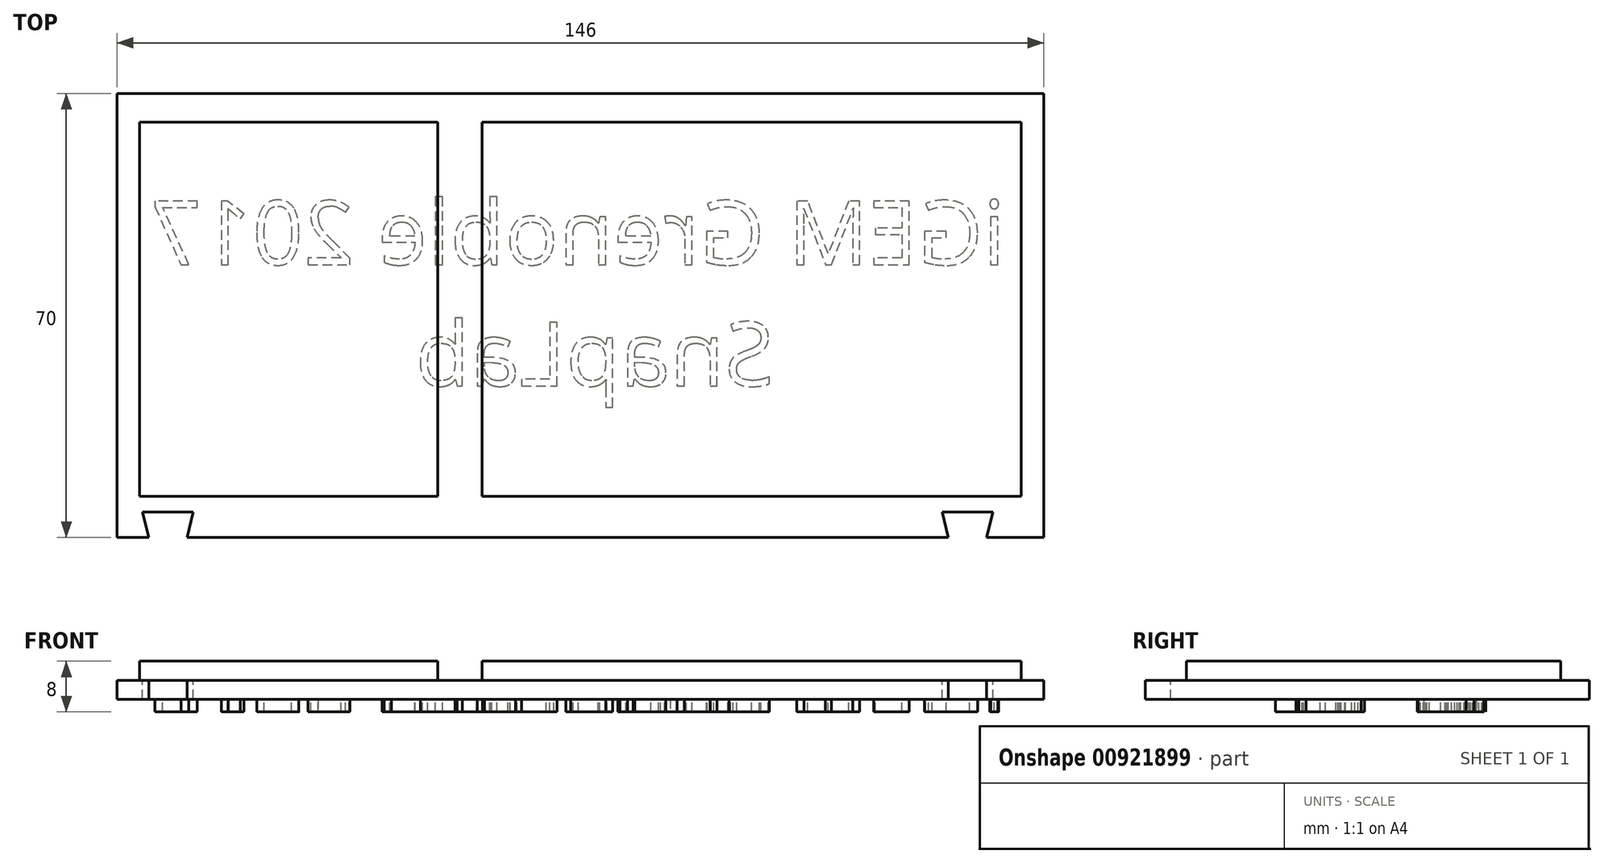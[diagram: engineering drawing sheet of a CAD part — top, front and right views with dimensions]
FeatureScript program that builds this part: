
annotation { "Feature Type Name" : "Feature", "Feature Type Description" : "" }
export const myFeature = defineFeature(function(context is Context, id is Id, definition is map)
    precondition{}
    {
        {
            var Q0;
            Q0=qCreatedBy(makeId("Top.planeOp"),FACE);
            var sketch = newSketch(context, id + "F0", { "sketchPlane" : qUnion([Q0])});
            skLineSegment(sketch, "E0.bottom", {"start": v(0, 0) * mm, "end": v(146, 0) * mm});
            skLineSegment(sketch, "E0.top", {"start": v(0, 70) * mm, "end": v(146, 70) * mm});
            skLineSegment(sketch, "E0.left", {"start": v(0, 0) * mm, "end": v(0, 70) * mm});
            skLineSegment(sketch, "E0.right", {"start": v(146, 0) * mm, "end": v(146, 70) * mm});
            skSolve(sketch);
        }
        {
            var Q0;
            Q0 = qSketchRegion(id + "F0", true);
            var Q1;
            Q1=makeQuery(id+"F0.imprint","IMPRINT",FACE,{"disambiguationData":[TD([[makeQuery(id+"F0.imprint","IMPRINT",EDGE,{"derivedFrom":sQuery(id+"F0.wireOp",EDGE,"E0.bottom")}),1.0]])]});
            extrude(context, id + "F1", {"entities" : qUnion([Q0, Q1]), "depth" : 3 * mm, "offsetDistance" : 25 * mm});
        }
        {
            var Q0;
            Q0=makeQuery(id+"F1.opExtrude","CAP_FACE",FACE,{"disambiguationData":[OSD([sQuery(id+"F0.wireOp",EDGE,"E0.bottom"),sQuery(id+"F0.wireOp",EDGE,"E0.top"),sQuery(id+"F0.wireOp",EDGE,"E0.left"),sQuery(id+"F0.wireOp",EDGE,"E0.right")])],"isStart":false});
            var sketch = newSketch(context, id + "F2", { "sketchPlane" : qUnion([Q0])});
            skLineSegment(sketch, "E1.bottom", {"start": v(3.5, 65.5) * mm, "end": v(50.5, 65.5) * mm});
            skLineSegment(sketch, "E1.top", {"start": v(3.5, 6.5) * mm, "end": v(50.5, 6.5) * mm});
            skLineSegment(sketch, "E1.left", {"start": v(3.5, 65.5) * mm, "end": v(3.5, 6.5) * mm});
            skLineSegment(sketch, "E1.right", {"start": v(50.5, 65.5) * mm, "end": v(50.5, 6.5) * mm});
            skLineSegment(sketch, "E2.bottom", {"start": v(57.5, 65.5) * mm, "end": v(142.5, 65.5) * mm});
            skLineSegment(sketch, "E2.top", {"start": v(57.5, 6.5) * mm, "end": v(142.5, 6.5) * mm});
            skLineSegment(sketch, "E2.left", {"start": v(57.5, 65.5) * mm, "end": v(57.5, 6.5) * mm});
            skLineSegment(sketch, "E2.right", {"start": v(142.5, 65.5) * mm, "end": v(142.5, 6.5) * mm});
            skLineSegment(sketch, "E3", {"start": v(4, 0) * mm, "end": v(4, 4) * mm});
            skLineSegment(sketch, "E4", {"start": v(4, 4) * mm, "end": v(12, 4) * mm});
            skLineSegment(sketch, "E5", {"start": v(12, 4) * mm, "end": v(12, 0) * mm});
            skLineSegment(sketch, "E6", {"start": v(138, 0) * mm, "end": v(138, 4) * mm});
            skLineSegment(sketch, "E7", {"start": v(138, 4) * mm, "end": v(130, 4) * mm});
            skLineSegment(sketch, "E8", {"start": v(130, 4) * mm, "end": v(130, 0) * mm});
            skLineSegment(sketch, "E9", {"start": v(4, 4) * mm, "end": v(5, 0) * mm});
            skLineSegment(sketch, "E10", {"start": v(5, 0) * mm, "end": v(4, 0) * mm});
            skLineSegment(sketch, "E11", {"start": v(12, 4) * mm, "end": v(11, 0) * mm});
            skLineSegment(sketch, "E12", {"start": v(11, 0) * mm, "end": v(12, 0) * mm});
            skLineSegment(sketch, "E13", {"start": v(138, 4) * mm, "end": v(137, 0) * mm});
            skLineSegment(sketch, "E14", {"start": v(137, 0) * mm, "end": v(138, 0) * mm});
            skLineSegment(sketch, "E15", {"start": v(130, 4) * mm, "end": v(131, 0) * mm});
            skLineSegment(sketch, "E16", {"start": v(131, 0) * mm, "end": v(130, 0) * mm});
            skSolve(sketch);
        }
        {
            var Q0;
            Q0=makeQuery(id+"F2.imprint","IMPRINT",FACE,{"disambiguationData":[TD([[makeQuery(id+"F2.imprint","IMPRINT",EDGE,{"derivedFrom":sQuery(id+"F2.wireOp",EDGE,"E1.bottom")}),-1.0]])]});
            var Q1;
            Q1=makeQuery(id+"F2.imprint","IMPRINT",FACE,{"disambiguationData":[TD([[makeQuery(id+"F2.imprint","IMPRINT",EDGE,{"derivedFrom":sQuery(id+"F2.wireOp",EDGE,"E2.bottom")}),-1.0]])]});
            extrude(context, id + "F3", {"entities" : qUnion([Q0, Q1]), "operationType" : NewBodyOperationType.ADD, "depth" : 3 * mm, "offsetDistance" : 25 * mm});
        }
        {
            var Q0;
            Q0=makeQuery(id+"F2.imprint","IMPRINT",FACE,{"disambiguationData":[TD([[makeQuery(id+"F2.imprint","IMPRINT",EDGE,{"derivedFrom":sQuery(id+"F2.wireOp",EDGE,"E4")}),-1.0]])]});
            extrude(context, id + "F4", {"entities" : qUnion([Q0]), "operationType" : NewBodyOperationType.REMOVE, "oppositeDirection" : true, "depth" : 3 * mm, "offsetDistance" : 25 * mm});
        }
        {
            var Q0;
            Q0=makeQuery(id+"F2.imprint","IMPRINT",FACE,{"disambiguationData":[TD([[makeQuery(id+"F2.imprint","IMPRINT",EDGE,{"derivedFrom":sQuery(id+"F2.wireOp",EDGE,"E7")}),1.0]])]});
            extrude(context, id + "F5", {"entities" : qUnion([Q0]), "operationType" : NewBodyOperationType.REMOVE, "oppositeDirection" : true, "depth" : 3 * mm, "offsetDistance" : 25 * mm});
        }
        {
            var Q0;
            Q0=makeQuery(id+"F1.opExtrude","CAP_FACE",FACE,{"disambiguationData":[OSD([sQuery(id+"F0.wireOp",EDGE,"E0.bottom"),sQuery(id+"F0.wireOp",EDGE,"E0.top"),sQuery(id+"F0.wireOp",EDGE,"E0.left"),sQuery(id+"F0.wireOp",EDGE,"E0.right")])],"isStart":true});
            var sketch = newSketch(context, id + "F6", { "sketchPlane" : qUnion([Q0])});
            skText(sketch, "E17", { "text": "iGEM Grenoble 2017\n          SnapLab", "fontName": "OpenSans-Regular.ttf"});
            const initialGuessF6  = {"E17": [0.14, -0.04303, -1, 0, 0.01012]};
            skSetInitialGuess(sketch, initialGuessF6);
            skSolve(sketch);
        }
        {
            var Q0;
            Q0=makeQuery(id+"F6.imprint","IMPRINT",FACE,{"disambiguationData":[TD([[makeQuery(id+"F6.imprint","IMPRINT",EDGE,{"derivedFrom":sQuery(id+"F6.wireOp",EDGE,"E17.sketch_text.stroke-4")}),-1.0]])]});
            var Q1;
            Q1=makeQuery(id+"F6.imprint","IMPRINT",FACE,{"disambiguationData":[TD([[makeQuery(id+"F6.imprint","IMPRINT",EDGE,{"derivedFrom":sQuery(id+"F6.wireOp",EDGE,"E17.sketch_text.stroke-12")}),-1.0]])]});
            var Q2;
            Q2=makeQuery(id+"F6.imprint","IMPRINT",FACE,{"disambiguationData":[TD([[makeQuery(id+"F6.imprint","IMPRINT",EDGE,{"derivedFrom":sQuery(id+"F6.wireOp",EDGE,"E17.sketch_text.stroke-32")}),-1.0]])]});
            var Q3;
            Q3=makeQuery(id+"F6.imprint","IMPRINT",FACE,{"disambiguationData":[TD([[makeQuery(id+"F6.imprint","IMPRINT",EDGE,{"derivedFrom":sQuery(id+"F6.wireOp",EDGE,"E17.sketch_text.stroke-0")}),-1.0]])]});
            var Q4;
            Q4=makeQuery(id+"F6.imprint","IMPRINT",FACE,{"disambiguationData":[TD([[makeQuery(id+"F6.imprint","IMPRINT",EDGE,{"derivedFrom":sQuery(id+"F6.wireOp",EDGE,"E17.sketch_text.stroke-44")}),-1.0]])]});
            var Q5;
            Q5=makeQuery(id+"F6.imprint","IMPRINT",FACE,{"disambiguationData":[TD([[makeQuery(id+"F6.imprint","IMPRINT",EDGE,{"derivedFrom":sQuery(id+"F6.wireOp",EDGE,"E17.sketch_text.stroke-62")}),-1.0]])]});
            var Q6;
            Q6=makeQuery(id+"F6.imprint","IMPRINT",FACE,{"disambiguationData":[TD([[makeQuery(id+"F6.imprint","IMPRINT",EDGE,{"derivedFrom":sQuery(id+"F6.wireOp",EDGE,"E17.sketch_text.stroke-82")}),-1.0]])]});
            var Q7;
            Q7=makeQuery(id+"F6.imprint","IMPRINT",FACE,{"disambiguationData":[TD([[makeQuery(id+"F6.imprint","IMPRINT",EDGE,{"derivedFrom":sQuery(id+"F6.wireOp",EDGE,"E17.sketch_text.stroke-95")}),-1.0]])]});
            var Q8;
            Q8=makeQuery(id+"F6.imprint","IMPRINT",FACE,{"disambiguationData":[TD([[makeQuery(id+"F6.imprint","IMPRINT",EDGE,{"derivedFrom":sQuery(id+"F6.wireOp",EDGE,"E17.sketch_text.stroke-114")}),-1.0]])]});
            var Q9;
            Q9=makeQuery(id+"F6.imprint","IMPRINT",FACE,{"disambiguationData":[TD([[makeQuery(id+"F6.imprint","IMPRINT",EDGE,{"derivedFrom":sQuery(id+"F6.wireOp",EDGE,"E17.sketch_text.stroke-131")}),-1.0]])]});
            var Q10;
            Q10=makeQuery(id+"F6.imprint","IMPRINT",FACE,{"disambiguationData":[TD([[makeQuery(id+"F6.imprint","IMPRINT",EDGE,{"derivedFrom":sQuery(id+"F6.wireOp",EDGE,"E17.sketch_text.stroke-148")}),-1.0]])]});
            var Q11;
            Q11=makeQuery(id+"F6.imprint","IMPRINT",FACE,{"disambiguationData":[TD([[makeQuery(id+"F6.imprint","IMPRINT",EDGE,{"derivedFrom":sQuery(id+"F6.wireOp",EDGE,"E17.sketch_text.stroke-171")}),-1.0]])]});
            var Q12;
            Q12=makeQuery(id+"F6.imprint","IMPRINT",FACE,{"disambiguationData":[TD([[makeQuery(id+"F6.imprint","IMPRINT",EDGE,{"derivedFrom":sQuery(id+"F6.wireOp",EDGE,"E17.sketch_text.stroke-175")}),-1.0]])]});
            var Q13;
            Q13=makeQuery(id+"F6.imprint","IMPRINT",FACE,{"disambiguationData":[TD([[makeQuery(id+"F6.imprint","IMPRINT",EDGE,{"derivedFrom":sQuery(id+"F6.wireOp",EDGE,"E17.sketch_text.stroke-194")}),-1.0]])]});
            var Q14;
            Q14=makeQuery(id+"F6.imprint","IMPRINT",FACE,{"disambiguationData":[TD([[makeQuery(id+"F6.imprint","IMPRINT",EDGE,{"derivedFrom":sQuery(id+"F6.wireOp",EDGE,"E17.sketch_text.stroke-214")}),-1.0]])]});
            var Q15;
            Q15=makeQuery(id+"F6.imprint","IMPRINT",FACE,{"disambiguationData":[TD([[makeQuery(id+"F6.imprint","IMPRINT",EDGE,{"derivedFrom":sQuery(id+"F6.wireOp",EDGE,"E17.sketch_text.stroke-230")}),-1.0]])]});
            var Q16;
            Q16=makeQuery(id+"F6.imprint","IMPRINT",FACE,{"disambiguationData":[TD([[makeQuery(id+"F6.imprint","IMPRINT",EDGE,{"derivedFrom":sQuery(id+"F6.wireOp",EDGE,"E17.sketch_text.stroke-239")}),-1.0]])]});
            var Q17;
            Q17=makeQuery(id+"F6.imprint","IMPRINT",FACE,{"disambiguationData":[TD([[makeQuery(id+"F6.imprint","IMPRINT",EDGE,{"derivedFrom":sQuery(id+"F6.wireOp",EDGE,"E17.sketch_text.stroke-246")}),-1.0]])]});
            var Q18;
            Q18=makeQuery(id+"F6.imprint","IMPRINT",FACE,{"disambiguationData":[TD([[makeQuery(id+"F6.imprint","IMPRINT",EDGE,{"derivedFrom":sQuery(id+"F6.wireOp",EDGE,"E17.sketch_text.stroke-271")}),-1.0]])]});
            var Q19;
            Q19=makeQuery(id+"F6.imprint","IMPRINT",FACE,{"disambiguationData":[TD([[makeQuery(id+"F6.imprint","IMPRINT",EDGE,{"derivedFrom":sQuery(id+"F6.wireOp",EDGE,"E17.sketch_text.stroke-288")}),-1.0]])]});
            var Q20;
            Q20=makeQuery(id+"F6.imprint","IMPRINT",FACE,{"disambiguationData":[TD([[makeQuery(id+"F6.imprint","IMPRINT",EDGE,{"derivedFrom":sQuery(id+"F6.wireOp",EDGE,"E17.sketch_text.stroke-315")}),-1.0]])]});
            var Q21;
            Q21=makeQuery(id+"F6.imprint","IMPRINT",FACE,{"disambiguationData":[TD([[makeQuery(id+"F6.imprint","IMPRINT",EDGE,{"derivedFrom":sQuery(id+"F6.wireOp",EDGE,"E17.sketch_text.stroke-340")}),-1.0]])]});
            var Q22;
            Q22=makeQuery(id+"F6.imprint","IMPRINT",FACE,{"disambiguationData":[TD([[makeQuery(id+"F6.imprint","IMPRINT",EDGE,{"derivedFrom":sQuery(id+"F6.wireOp",EDGE,"E17.sketch_text.stroke-346")}),-1.0]])]});
            var Q23;
            Q23=makeQuery(id+"F6.imprint","IMPRINT",FACE,{"disambiguationData":[TD([[makeQuery(id+"F6.imprint","IMPRINT",EDGE,{"derivedFrom":sQuery(id+"F6.wireOp",EDGE,"E17.sketch_text.stroke-373")}),-1.0]])]});
            extrude(context, id + "F7", {"entities" : qUnion([Q0, Q1, Q2, Q3, Q4, Q5, Q6, Q7, Q8, Q9, Q10, Q11, Q12, Q13, Q14, Q15, Q16, Q17, Q18, Q19, Q20, Q21, Q22, Q23]), "operationType" : NewBodyOperationType.ADD, "depth" : 2 * mm, "offsetDistance" : 25 * mm});
        }
    });
